# Revit family: R1200-RB
name_source: partatom
category: Plumbing Fixtures
revit_build: Autodesk Revit 2018 (Build: 20170223_1515(x64)
units: mm (PartAtom-declared; Revit-internal decimal feet)

## family parameters
Cut with Voids When Loaded = No
Host = Face
Part Type = Normal
Room Calculation Point = No
Round Connector Dimension = Use Radius
Shared = No

## types (6) — shared parameters
Costom Height = 0' - 7 1/2"
Default Elevation = 0' - 0"
Description = LARGE SUMP PROMENADE DECK DRAIN WITH ADJUSTABLE EXTENSION AND 12 ¾" x 12 ¾" SECURED TOP ASSEMBLY
Floor Drain Material = Paint - Sherwin Williams Paint - #952C2A - Bellwood Red
Manufacturer = MIFAB
URL = WWW.MIFAB.COM
zero-valued in all types: CWFU, WFU

## per-type parameters (varying)
| type | Model | Pipe Diameter | Pipe Radius |
| R1208-RB_Drain Pipe Size 8" | R1208-RB | 0' - 8" | 0' - 4" |
| R1205-RB_Drain Pipe Size 5" | R1205-RB | 0' - 5" | 0' - 2 1/2" |
| R1204-RB_Drain Pipe Size 4" | R1204-RB | 0' - 4" | 0' - 2" |
| R1203-RB_Drain Pipe Size 3" | R1203-RB | 0' - 3" | 0' - 1 1/2" |
| R1202-RB_Drain Pipe Size 2" | R1202-RB | 0' - 2" | 0' - 1" |
| R1206-RB_Drain Pipe Size 6" | R1206-RB | 0' - 6" | 0' - 3" |

## geometry (parser evidence)
native form markers: Blend x4, Sweep x8
no freeform markers — native parametric forms only
